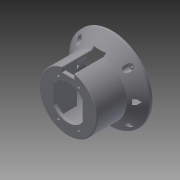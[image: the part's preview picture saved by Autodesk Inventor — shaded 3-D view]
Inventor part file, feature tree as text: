
AUTODESK INVENTOR PART (.ipt)
format: ipt  version: 2014 SP2 (Build 180246200, 246)  size: 368,640 bytes
history: native  units: mm
features: extrude x14, sketch x14, chamfer x5, fillet x3
ambient origin geometry x8: Origin, YZ Plane, XZ Plane, XY Plane, X Axis, Y Axis, Z Axis, Center Point
bodies: Solid1 (feature_tree)
feature tree (36):
  extrude  "Extrusion1"  Depth=71.0mm
  extrude  "Extrusion2"  Depth=3.0mm
  extrude  "Extrusion3"  Depth=52.5mm
  extrude  "Extrusion5"  Depth=12.5mm
  chamfer  "Chamfer2"  Distance=5.0mm
  extrude  "Extrusion4"  Depth=7.0mm
  extrude  "Extrusion6"  Depth=71.0mm
  extrude  "Extrusion7"  Depth=71.0mm
  extrude  "Extrusion8"  Depth=3.0mm TaperAngle=0.0deg
  fillet  "Fillet1"  Radius=36.0mm
  extrude  "Extrusion9"  Depth=27.0mm
  extrude  "Extrusion10"  Depth=3.0mm
  extrude  "Extrusion11"  Depth=3.0mm
  extrude  "Extrusion12"  Depth=54.0mm
  extrude  "Extrusion13"  Depth=27.0mm
  extrude  "Extrusion14"  Depth=25.0mm TaperAngle=0.0deg
  chamfer  "Chamfer3"  Distance=6.0mm
  chamfer  "Chamfer4"  Distance=3.0mm
  chamfer  "Chamfer5"  Distance=46.0mm
  chamfer  "Chamfer6"  Distance=6.0mm
  fillet  "Fillet2"  Radius=150.0mm
  fillet  "Fillet3"  Radius=6.0mm
  sketch  "Sketch1"  dims[d0=43.0mm d1=71.0mm]
  sketch  "Sketch2"  dims[d4=4.0mm d5=0.0mm d6=3.0mm]
  sketch  "Sketch3"  dims[d7=47.0mm d8=0.0mm d9=52.5mm]
  sketch  "Sketch4"  dims[d10=25.0mm d11=12.5mm]
  sketch  "Sketch5"  dims[d12=3.5mm]
  sketch  "Sketch6"  dims[d13=3.5mm]
  sketch  "Sketch7"  dims[d14=3.5mm]
  sketch  "Sketch8"  dims[d15=3.5mm d16=5.0mm d17=0.0mm]
  sketch  "Sketch9"  dims[d18=14.0mm d19=7.0mm]
  sketch  "Sketch10"  dims[d20=29.0mm d21=71.0mm]
  sketch  "Sketch11"  dims[d22=100.0mm d23=0.0mm d27=71.0mm]
  sketch  "Sketch12"  dims[d28=100.0mm d29=3.0mm d30=0.0mm]
  sketch  "Sketch13"  dims[d31=14.5mm d32=2.0mm d33=45.0deg d34=36.0mm]
  sketch  "Sketch14"  dims[d35=54.0mm d36=27.0mm d37=3.0mm d38=3.0mm d39=54.0mm d40=27.0mm d41=25.0mm d42=0.0mm d43=6.0mm d44=3.0mm d45=46.0mm d46=6.0mm d47=150.0mm d48=0.0mm d49=6.0mm d50=6.0mm d51=40.0mm d52=110.0mm d53=0.0mm d54=3.0mm d55=7.0mm d56=6.0mm d57=6.0mm d58=3.0mm d59=46.0mm d60=150.0mm d61=0.0mm d62=85.0mm d63=8.0mm d64=8.0mm d65=8.0mm d66=8.0mm d67=96.0mm d68=0.0mm d69=3.5mm d70=96.0mm d71=0.0mm d72=3.5mm d73=96.0mm d74=0.0mm d75=3.5mm d76=96.0mm d77=0.0mm d78=3.5mm d79=96.0mm d80=0.0mm d81=3.0mm d82=2.0mm d83=45.0deg d84=3.0mm d85=2.0mm d86=45.0deg d87=3.0mm d88=2.0mm d89=45.0deg d90=3.0mm d91=2.0mm d92=45.0deg d93=1.0mm d94=1.0mm]
